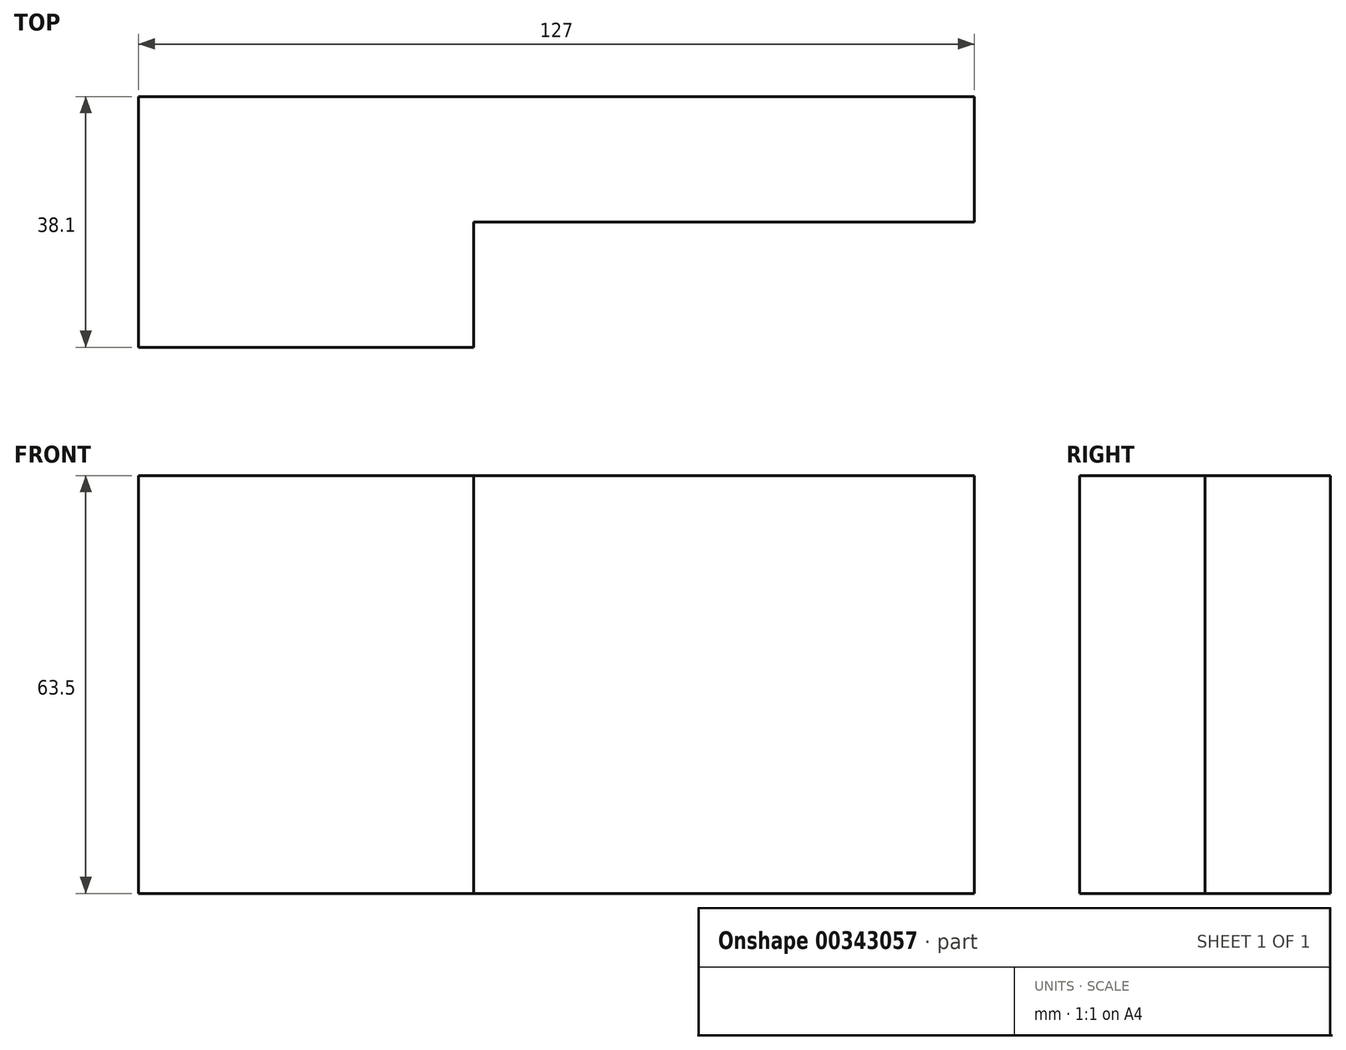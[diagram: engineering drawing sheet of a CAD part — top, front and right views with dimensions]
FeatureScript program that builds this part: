
annotation { "Feature Type Name" : "Feature", "Feature Type Description" : "" }
export const myFeature = defineFeature(function(context is Context, id is Id, definition is map)
    precondition{}
    {
        {
            var Q0;
            Q0=qCreatedBy(makeId("Top.planeOp"),FACE);
            var sketch = newSketch(context, id + "F0", { "sketchPlane" : qUnion([Q0])});
            skLineSegment(sketch, "E0", {"start": v(-70.2, 101.6) * mm, "end": v(56.8, 101.6) * mm});
            skLineSegment(sketch, "E1", {"start": v(-70.2, 101.6) * mm, "end": v(-70.2, 63.5) * mm});
            skLineSegment(sketch, "E2", {"start": v(-70.2, 63.5) * mm, "end": v(-19.24, 63.5) * mm});
            skLineSegment(sketch, "E3", {"start": v(-19.24, 63.5) * mm, "end": v(-19.24, 82.55) * mm});
            skLineSegment(sketch, "E4", {"start": v(56.8, 101.6) * mm, "end": v(56.8, 82.55) * mm});
            skLineSegment(sketch, "E5", {"start": v(56.8, 82.55) * mm, "end": v(-19.24, 82.55) * mm});
            skSolve(sketch);
        }
        {
            var Q0;
            Q0 = qSketchRegion(id + "F0", true);
            extrude(context, id + "F1", {"entities" : qUnion([Q0]), "depth" : 63.5 * mm});
        }
    });
